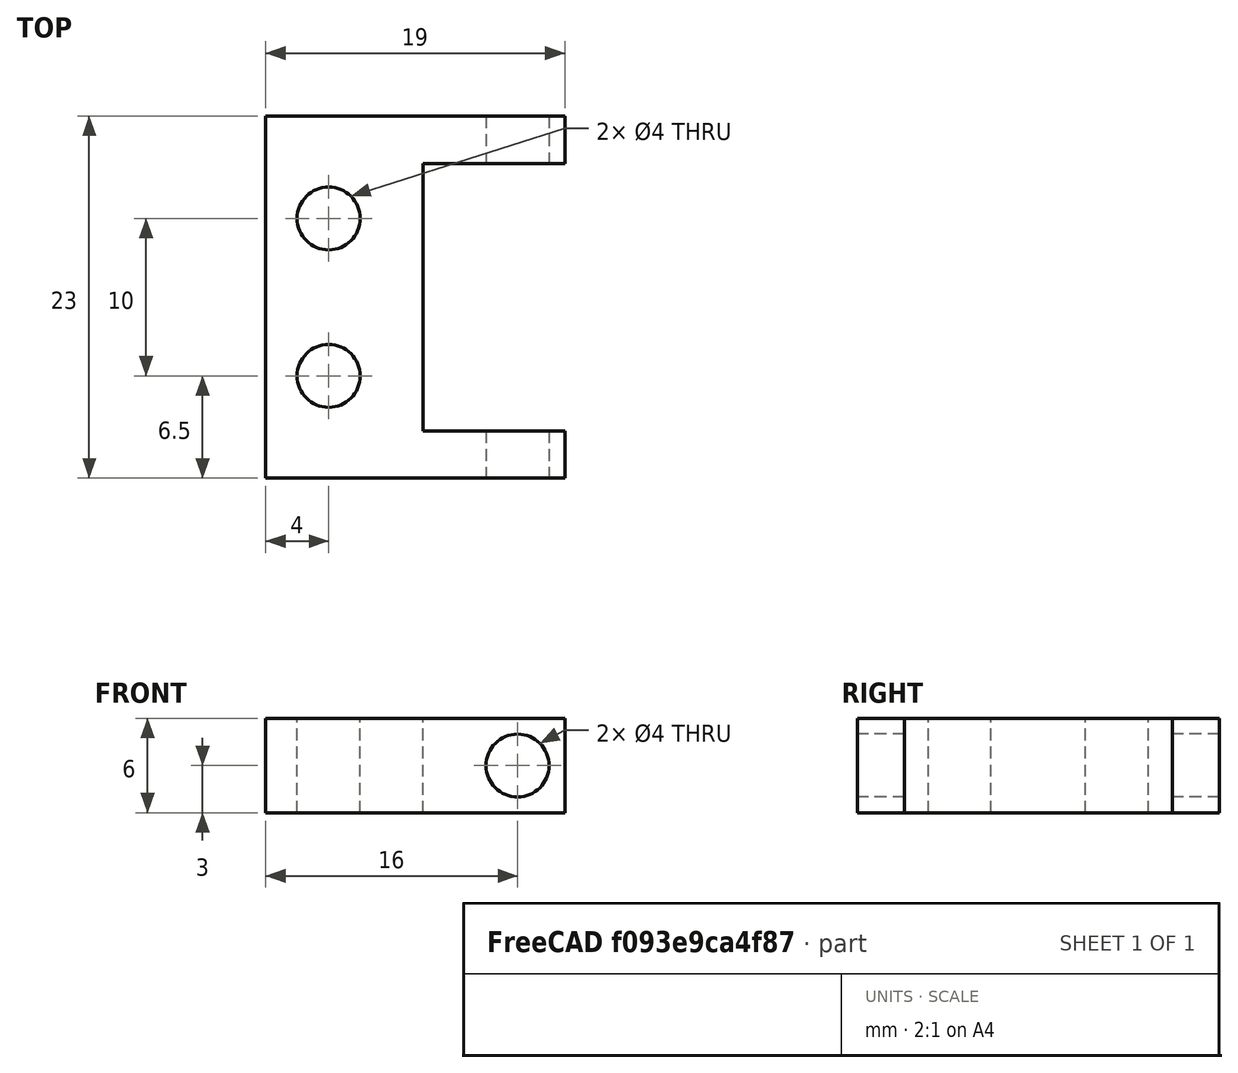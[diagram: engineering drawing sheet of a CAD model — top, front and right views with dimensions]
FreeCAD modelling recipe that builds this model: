
FCSTD DOCUMENT  (FreeCAD 0.14R3702 (Git))
Label: camera base plate
License: CC-BY 3.0
LicenseURL: http://creativecommons.org/licenses/by/3.0/
objects: Part::Cylinder×4, Part::Cut×4, Part::Box×3, Part::MultiFuse×1
note: 12 computed .brp shape members not serialized (recipe doc carries the construction recipe); baked Part::Feature solids carry a one-line shape summary decoded from their .brp

FEATURE [Part::Box] Box  label="Cube"
  Height = 6
  Length = 10
  Width = 17
FEATURE [Part::Cylinder] Cylinder
  Angle = 360
  Height = 10
  Placement = pos=(4,3.5,0) rot=(0,0,1;0rad)
  Radius = 2
FEATURE [Part::Cylinder] Cylinder001
  Angle = 360
  Height = 10
  Placement = pos=(4,3.5,0) rot=(0,0,1;0rad)
  Radius = 2
FEATURE [Part::Cut] Cut
  Base = -> Box
  Tool = -> Cylinder
FEATURE [Part::Cut] Cut001
  Base = -> Cut
  Tool = -> Cylinder001
FEATURE [Part::Cylinder] Cylinder002
  Angle = 360
  Height = 10
  Placement = pos=(4,13.5,0) rot=(0,0,1;0rad)
  Radius = 2
FEATURE [Part::Cut] Cut002
  Base = -> Cut001
  Tool = -> Cylinder002
FEATURE [Part::Box] Box001  label="Cube001"
  Height = 6
  Length = 19
  Placement = pos=(0,-3,0) rot=(0,0,1;0rad)
  Width = 3
FEATURE [Part::Box] Box002  label="Cube002"
  Height = 6
  Length = 19
  Placement = pos=(0,17,0) rot=(0,0,1;0rad)
  Width = 3
FEATURE [Part::Cylinder] Cylinder003
  Angle = 360
  Height = 25
  Placement = pos=(16,21,3) rot=(1,0,0;1.5708rad)
  Radius = 2
FEATURE [Part::MultiFuse] Fusion
  Shapes = -> [Cut002,Box001,Box002]
FEATURE [Part::Cut] Cut003
  Base = -> Fusion
  Tool = -> Cylinder003
